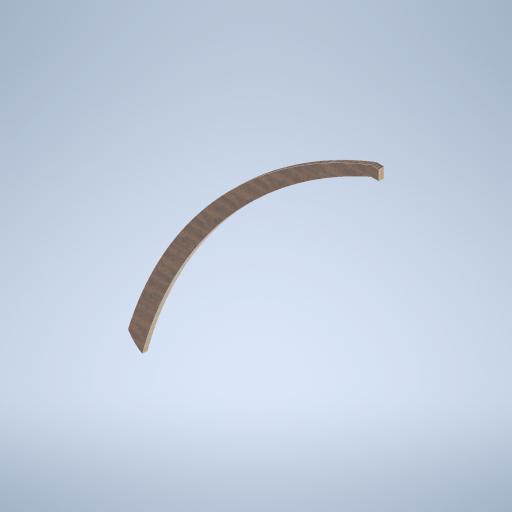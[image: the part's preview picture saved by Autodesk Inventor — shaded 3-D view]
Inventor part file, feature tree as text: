
AUTODESK INVENTOR PART (.ipt)
format: ipt  version: 2024.2 (Build 282272000, 272)  size: 269,824 bytes
history: native  units: mm
features: extrude x1
ambient origin geometry x8: Origin, YZ Plane, XZ Plane, XY Plane, X Axis, Y Axis, Z Axis, Center Point
bodies: Solid1 (feature_tree)
feature tree (1):
  extrude  "Extrusion1"  Depth=100.0mm TaperAngle=0.0deg
